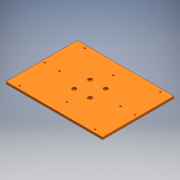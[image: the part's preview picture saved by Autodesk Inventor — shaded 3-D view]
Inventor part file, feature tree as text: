
AUTODESK INVENTOR PART (.ipt)
format: ipt  version: 2016 (Build 200138000, 138)  size: 177,152 bytes
history: native  units: mm
features: sketch x4, extrude x2, hole x2, mirror x2
ambient origin geometry x8: Origin, YZ Plane, XZ Plane, XY Plane, X Axis, Y Axis, Z Axis, Center Point
bodies: Solid1 (feature_tree)
feature tree (10):
  extrude  "baseExtrusion"  Depth=85.05mm
  hole  "zStageM6MountingHoles"  [1 undecoded]
  extrude  "excessExtrusion"  Depth=10.0mm
  hole  "Hole4"  [1 undecoded]
  mirror  "Mirror7"
  mirror  "Mirror8"
  sketch  "Sketch1"  dims[d0=170.1mm d1=85.05mm]
  sketch  "Sketch2"  dims[d2=109.4mm d3=54.7mm]
  sketch  "Sketch5"  dims[d4=10.0mm d5=0.0mm d7=75.0mm]
  sketch  "Sketch7"  dims[d9=37.5mm d10=6.6mm d11=6.0mm d12=18.0mm d13=6.6mm d14=90.0deg d15=8.0mm d16=20.594885mm d33=10.0mm d34=0.0mm d44=340.0mm d45=170.0mm d46=460.0mm d47=230.0mm d48=15.0mm d50=15.0mm d51=85.0mm d53=6.6mm d54=6.0mm d55=18.0mm d56=4.8mm d57=90.0deg d58=8.0mm d59=20.594885mm d60=50.0mm d61=60.0mm d62=75.0mm d63=37.5mm]
note: 2 required parameter values undecoded (feature->parameter linkage not recoverable at this tier; creation-order binding heuristic only, values carry confidence <= 0.55)
